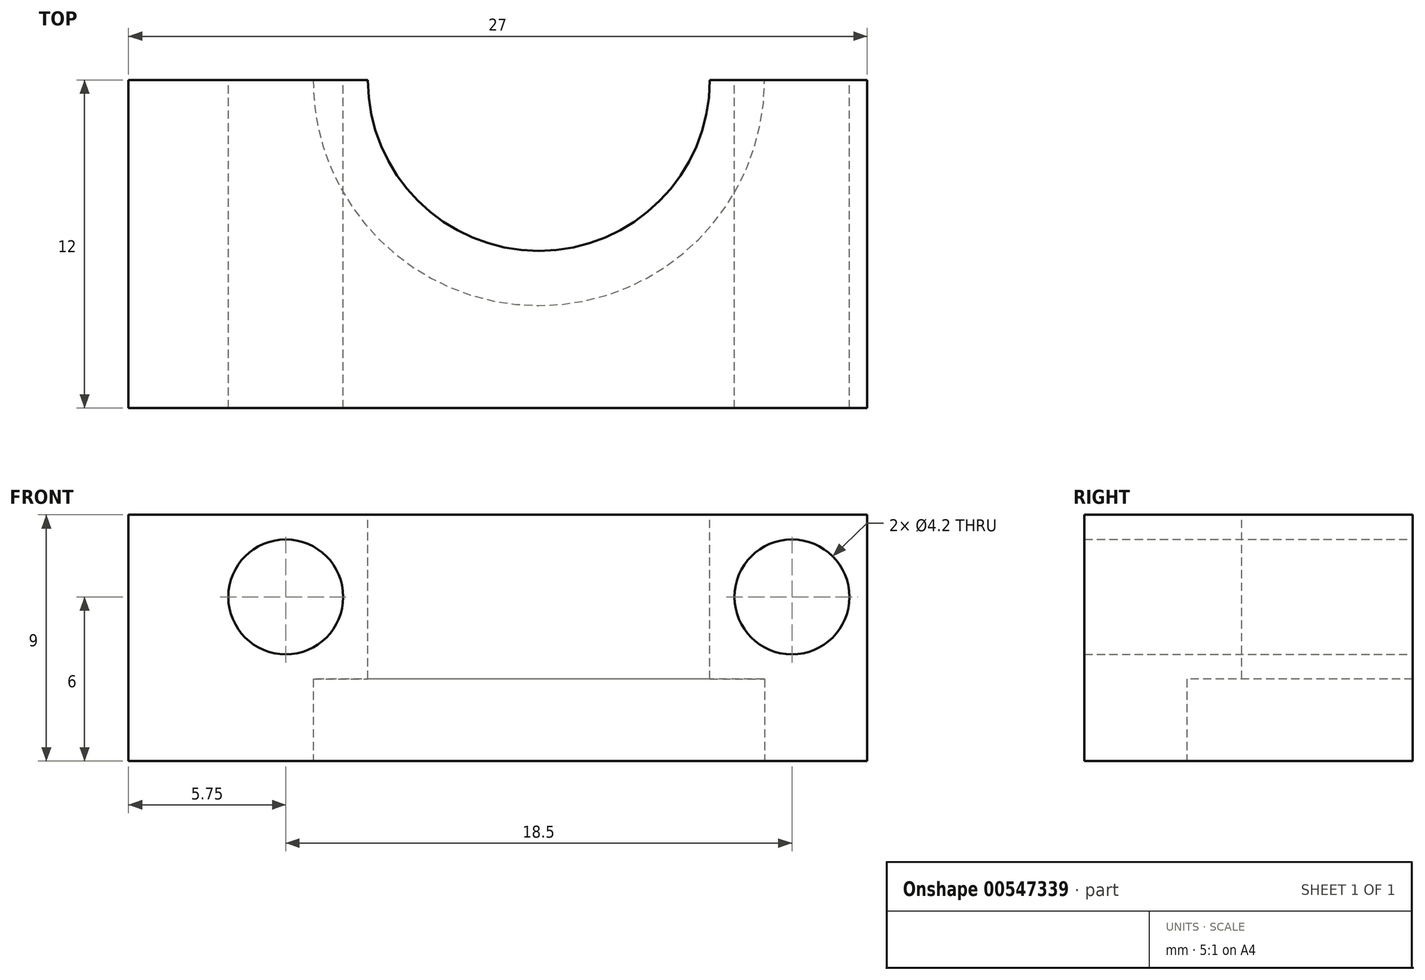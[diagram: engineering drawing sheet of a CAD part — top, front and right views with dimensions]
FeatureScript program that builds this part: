
annotation { "Feature Type Name" : "Feature", "Feature Type Description" : "" }
export const myFeature = defineFeature(function(context is Context, id is Id, definition is map)
    precondition{}
    {
        {
            var Q0;
            Q0=qCreatedBy(makeId("Front.planeOp"),FACE);
            var sketch = newSketch(context, id + "F0", { "sketchPlane" : qUnion([Q0])});
            skLineSegment(sketch, "E0.bottom", {"start": v(-15, 0) * mm, "end": v(12, 0) * mm});
            skLineSegment(sketch, "E0.top", {"start": v(-15, 9) * mm, "end": v(12, 9) * mm});
            skLineSegment(sketch, "E0.left", {"start": v(-15, 0) * mm, "end": v(-15, 9) * mm});
            skLineSegment(sketch, "E0.right", {"start": v(12, 0) * mm, "end": v(12, 9) * mm});
            skSolve(sketch);
        }
        {
            var Q0;
            Q0 = qSketchRegion(id + "F0", true);
            extrude(context, id + "F1", {"entities" : qUnion([Q0]), "depth" : 12 * mm, "offsetDistance" : 25 * mm});
        }
        {
            var Q0;
            Q0=makeQuery(id+"F1.opExtrude","SWEPT_FACE",FACE,{"disambiguationData":[OSD([sQuery(id+"F0.wireOp",EDGE,"E0.top")])]});
            var sketch = newSketch(context, id + "F2", { "sketchPlane" : qUnion([Q0])});
            skCircle(sketch, "E1", {"center": v(0, 0) * mm, "radius": 6.25 * mm});
            skSolve(sketch);
        }
        {
            var Q0;
            Q0 = qSketchRegion(id + "F2", true);
            extrude(context, id + "F3", {"entities" : qUnion([Q0]), "operationType" : NewBodyOperationType.REMOVE, "endBound" : BoundingType.THROUGH_ALL, "oppositeDirection" : true, "depth" : 25 * mm, "offsetDistance" : 25 * mm});
        }
        {
            var Q0;
            Q0=makeQuery(id+"F1.opExtrude","SWEPT_FACE",FACE,{"disambiguationData":[OSD([sQuery(id+"F0.wireOp",EDGE,"E0.bottom")])]});
            var sketch = newSketch(context, id + "F4", { "sketchPlane" : qUnion([Q0])});
            skCircle(sketch, "E2", {"center": v(0, 0) * mm, "radius": 8.25 * mm});
            skSolve(sketch);
        }
        {
            var Q0;
            Q0 = qSketchRegion(id + "F4", true);
            extrude(context, id + "F5", {"entities" : qUnion([Q0]), "operationType" : NewBodyOperationType.REMOVE, "oppositeDirection" : true, "depth" : 3 * mm, "offsetDistance" : 25 * mm});
        }
        {
            var Q0;
            {var subQ0=sQuery(id+"F0.wireOp",EDGE,"E0.bottom");var subQ1=sQuery(id+"F0.wireOp",EDGE,"E0.right");var subQ2=sQuery(id+"F0.wireOp",EDGE,"E0.top");Q0=makeQuery(id+"F3.boolean.opBoolean","SPLIT",FACE,{"disambiguationData":[TD([makeQuery(id+"F1.opExtrude","SWEPT_FACE",FACE,{"disambiguationData":[OSD([subQ1])]})])],"derivedFrom":makeQuery(id+"F1.opExtrude","CAP_FACE",FACE,{"disambiguationData":[OSD([subQ0,subQ2,sQuery(id+"F0.wireOp",EDGE,"E0.left"),subQ1])],"isStart":true})});}
            var sketch = newSketch(context, id + "F6", { "sketchPlane" : qUnion([Q0])});
            skCircle(sketch, "E3", {"center": v(-9.25, 6) * mm, "radius": 2.1 * mm});
            skCircle(sketch, "E4.MirrorC", {"center": v(9.25, 6) * mm, "radius": 2.1 * mm});
            skSolve(sketch);
        }
        {
            var Q0;
            Q0 = qSketchRegion(id + "F6", true);
            extrude(context, id + "F7", {"entities" : qUnion([Q0]), "operationType" : NewBodyOperationType.REMOVE, "endBound" : BoundingType.THROUGH_ALL, "oppositeDirection" : true, "depth" : 25 * mm, "offsetDistance" : 25 * mm});
        }
    });
